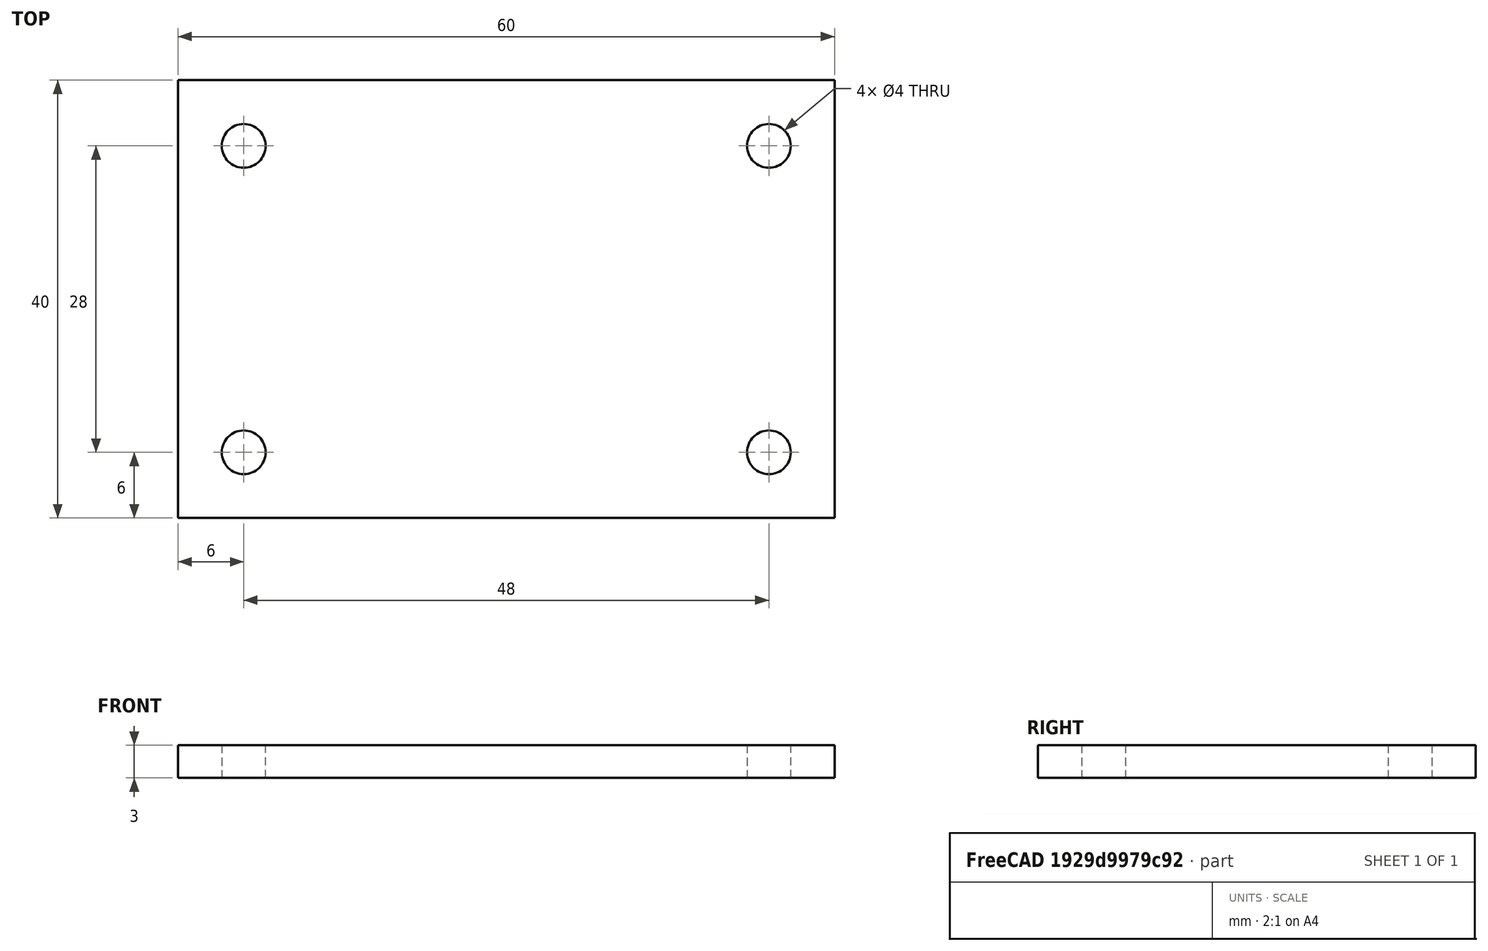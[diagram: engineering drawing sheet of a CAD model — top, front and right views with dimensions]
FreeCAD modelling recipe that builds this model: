
FCSTD DOCUMENT  (FreeCAD 0.21R33771 (Git))
Label: OJT1_T19P01_restriccions simetria
License: All rights reserved
LicenseURL: http://en.wikipedia.org/wiki/All_rights_reserved
objects: Sketcher::SketchObject×1, PartDesign::Pad×1, PartDesign::Body×1
note: 4 computed .brp shape members not serialized (recipe doc carries the construction recipe); baked Part::Feature solids carry a one-line shape summary decoded from their .brp

FEATURE [Sketcher::SketchObject] Sketch
  FullyConstrained = true
  MapMode = 5
  Support = -> [XY_Plane]
  sketch-geometry (8):
    g0: LineSegment StartX=-30 StartY=20 StartZ=0 EndX=30 EndY=20 EndZ=0
    g1: LineSegment StartX=30 StartY=20 StartZ=0 EndX=30 EndY=-20 EndZ=0
    g2: LineSegment StartX=30 StartY=-20 StartZ=0 EndX=-30 EndY=-20 EndZ=0
    g3: LineSegment StartX=-30 StartY=-20 StartZ=0 EndX=-30 EndY=20 EndZ=0
    g4: Circle CenterX=-24 CenterY=14 CenterZ=0 NormalX=0 NormalY=0 NormalZ=1 AngleXU=0 Radius=2
    g5: Circle CenterX=24 CenterY=14 CenterZ=0 NormalX=0 NormalY=0 NormalZ=1 AngleXU=0 Radius=2
    g6: Circle CenterX=-24 CenterY=-14 CenterZ=0 NormalX=0 NormalY=0 NormalZ=1 AngleXU=0 Radius=2
    g7: Circle CenterX=24 CenterY=-14 CenterZ=0 NormalX=0 NormalY=0 NormalZ=1 AngleXU=0 Radius=2
  constraints (19):
    c: Coincident(g0,g1)
    c: Coincident(g1,g2)
    c: Coincident(g2,g3)
    c: Coincident(g3,g0)
    c: Horizontal(g2)
    c: Vertical(g1)
    c: Symmetric(g0,g0,g-2)
    c: Symmetric(g0,g2,g-1)
    c: Equal(g4,g6)
    c: Equal(g6,g5)
    c: Equal(g5,g7)
    c: Symmetric(g4,g5,g-2)
    c: Symmetric(g6,g7,g-2)
    c: Symmetric(g4,g6,g-1)
    c: DistanceX(g0,g4) = 6
    c: DistanceY(g4,g0) = 6
    c: Radius(g4) = 2
    c: DistanceX(g2,g1) = 60
    c: DistanceY(g2,g0) = 40
FEATURE [PartDesign::Pad] Pad
  Direction = (0,0,1)
  Length = 3
  Length2 = 10
  Profile = -> Sketch
  ReferenceAxis = -> Sketch [N_Axis]
  Type = 0
FEATURE [PartDesign::Body] Body
  Group = -> [Sketch,Pad]
  Origin = -> Origin
  Tip = -> Pad
